# Revit family: GNW_A3-AU-Casement-01-In-trim-3-2
name_source: partatom
category: Windows
revit_build: Autodesk Revit 2016 (Build: 20150220_1215(x64)
units: mm (PartAtom-declared; Revit-internal decimal feet)

## family parameters
Always vertical = Yes
Cut with Voids When Loaded = No
Host = Wall
Room Calculation Point = No
Shared = No

## types (8) — shared parameters
Frame thickness = 40 mm
Head height = 2100 mm
Rebate depth = 10 mm  [stored 0.0328084 ft]
Trim thickness = 20 mm
Wall Closure = By host

## per-type parameters (varying)
| type | Default Sill Height | Depth | Frame width | Height | Width |
| 2770x1800 Casement | 300 mm | 1800 mm  [stored 5.90551 ft] | 90 mm  [stored 0.295276 ft] | 1800 mm  [stored 5.90551 ft] | 2770 mm |
| 2770x2100 Casement | 0 mm  [stored 0 ft] | 2100 mm | 90 mm  [stored 0.295276 ft] | 2100 mm | 2770 mm |
| 2410x1800 Casement | 300 mm | 1800 mm  [stored 5.90551 ft] | 120 mm  [stored 0.393701 ft] | 1800 mm  [stored 5.90551 ft] | 2410 mm  [stored 7.90682 ft] |
| 2410x2100 Casement | 0 mm  [stored 0 ft] | 2100 mm | 90 mm  [stored 0.295276 ft] | 2100 mm | 2410 mm  [stored 7.90682 ft] |
| 2050x1800 Casement | 300 mm | 1800 mm  [stored 5.90551 ft] | 90 mm  [stored 0.295276 ft] | 1800 mm  [stored 5.90551 ft] | 2050 mm |
| 2050x2100 Casement | 0 mm  [stored 0 ft] | 2100 mm | 90 mm  [stored 0.295276 ft] | 2100 mm | 2050 mm |
| 1810x1800 Casement | 300 mm | 1800 mm  [stored 5.90551 ft] | 90 mm  [stored 0.295276 ft] | 1800 mm  [stored 5.90551 ft] | 1810 mm |
| 1810x2100 Casement | 0 mm  [stored 0 ft] | 2100 mm | 90 mm  [stored 0.295276 ft] | 2100 mm | 1810 mm |

note: [stored X ft] marks values corroborated as IEEE doubles in the binary element streams (Revit-internal decimal feet)

## geometry (parser evidence)
native form markers: Sweep x1
no freeform markers — native parametric forms only
